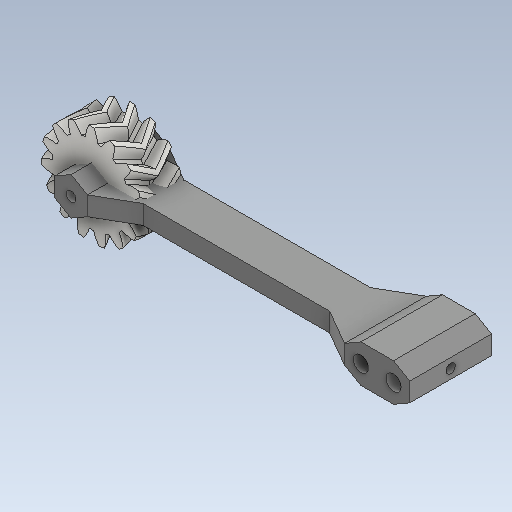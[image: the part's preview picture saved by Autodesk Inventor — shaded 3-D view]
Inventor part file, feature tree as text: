
AUTODESK INVENTOR PART (.ipt)
format: ipt  version: 2020 (Build 240168000, 168)  size: 989,696 bytes
history: native  units: in
note: dims shown in document units (in); Inventor stores cm internally (conversion verified against a paired STEP export)
features: sketch x5, extrude x4, other x3, plane x2, mirror x1, projected_geometry x1
ambient origin geometry x8: Origin, YZ Plane, XZ Plane, XY Plane, X Axis, Y Axis, Z Axis, Center Point
bodies: Solid1 (feature_tree), Solid2 (feature_tree)
feature tree (16):
  other  "Spur Gear1"
  plane  "Work Plane3"
  extrude  "Extrusion1"  Depth=3.4256in
  plane  "Work Plane1"
  extrude  "Extrusion2"  Depth=0.7874in
  sketch  "Sketch4"  dims[d4=0.0in d5=0.0906in]
  extrude  "Extrusion4"  Depth=0.0906in
  mirror  "Mirror3"
  extrude  "Extrusion11"  Depth=0.315in
  sketch  "Sketch1"  dims[d0=0.1818in d1=3.4256in]
  sketch  "Sketch2"  dims[d2=0.0945in d3=0.7874in]
  sketch  "Sketch5"  dims[d6=0.7874in d7=0.0in d29=0.315in]
  other  "Solid1::Spur Gear1"
  other  "TaggingFeature1"
  projected_geometry  "Projected Loop11"
  sketch  "Sketch15"  dims[d31=0.315in d33=0.1476in d34=0.2362in d35=0.0in d38=0.315in d69=2.4807in d70=0.3937in d71=0.1969in d79=0.0in d80=0.3937in d81=0.0in]
